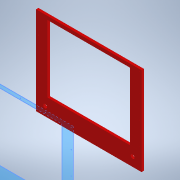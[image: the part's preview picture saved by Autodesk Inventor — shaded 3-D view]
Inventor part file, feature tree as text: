
AUTODESK INVENTOR PART (.ipt)
format: ipt  version: 2022 (Build 260153000, 153)  size: 146,944 bytes
history: native  units: mm
features: reference x11, other x9, mirror x2, sketch x2, extrude x1, hole x1
ambient origin geometry x8: Origin, YZ Plane, XZ Plane, XY Plane, X Axis, Y Axis, Z Axis, Center Point
bodies: Solid1 (feature_tree)
feature tree (26):
  extrude  "Extrusion1"  Depth=12.0mm TaperAngle=0.0deg
  hole  "Hole1"  [1 undecoded]
  mirror  "Mirror1"
  mirror  "Mirror2"
  sketch  "Sketch1"  dims[d0=1.0mm d1=12.0mm d2=0.0mm]
  reference  "Reference1"
  reference  "Reference2"
  reference  "Reference3"
  reference  "Reference4"
  reference  "Reference5"
  reference  "Reference6"
  reference  "Reference7"
  reference  "Reference8"
  reference  "Reference9"
  reference  "Reference10"
  reference  "Reference11"
  sketch  "Sketch2"  dims[d3=10.0mm d4=10.0mm d5=2.0mm d6=6.0mm d7=4.0mm d8=2.0mm d9=90.0deg d10=8.0mm d11=20.594885mm]
  other  "<userpath>\Documents\Inventor\lehman\Assembly1.iam"
  other  "Assembly1.iam"
  other  "lag2:1"
  other  "skærm:1"
  other  "<userpath>\Documents\Inventor\etchasketch\etchasketch.iam"
  other  "etchasketch.iam"
  other  "Knobass:1"
  other  "BS 290 SKF 626:1"
  other  "Knobass:2"
note: 1 required parameter value undecoded (feature->parameter linkage not recoverable at this tier; creation-order binding heuristic only, values carry confidence <= 0.55)
